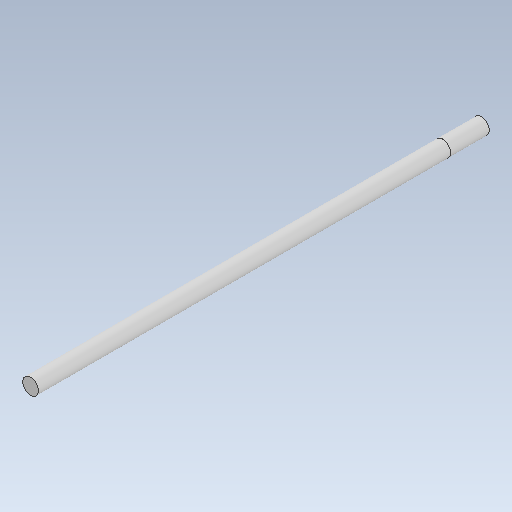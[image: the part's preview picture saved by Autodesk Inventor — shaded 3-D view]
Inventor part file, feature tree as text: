
AUTODESK INVENTOR PART (.ipt)
format: ipt  version: 2021 (Build 250183000, 183)  size: 102,912 bytes
history: native  units: mm
features: sketch x4, extrude x3
ambient origin geometry x8: Origin, YZ Plane, XZ Plane, XY Plane, X Axis, Y Axis, Z Axis, Center Point
bodies: Solid1 (feature_tree)
feature tree (7):
  extrude  "Extrusion1"  Depth=75.0mm TaperAngle=0.0deg
  sketch  "Sketch2"  dims[d3=10.0mm d4=0.0mm d5=8.0mm d6=0.0mm]
  extrude  "Extrusion2"  Depth=8.0mm TaperAngle=0.0deg
  extrude  "Extrusion3"  [1 undecoded]
  sketch  "Sketch1"  dims[d0=3.28mm d1=75.0mm d2=0.0mm]
  sketch  "Sketch3"
  sketch  "Sketch4"
note: 1 required parameter value undecoded (feature->parameter linkage not recoverable at this tier; creation-order binding heuristic only, values carry confidence <= 0.55)
